# Revit family: IS_Tesi_A6557_BIM_DE
name_source: partatom
category: Plumbing Fixtures
revit_build: Autodesk Revit MEP 2015 (Build: 20140606_1530(x64)
units: mm (PartAtom-declared; Revit-internal decimal feet)

## types (1)
- A6557AA - TESI single lever basin mixer with pop-up waste
    Assembly Code = C1030200
    BIMobject category = Taps & Mixers
    BOSUseNativeGeometries = 1
    Brand url = http://www.idealstandard.co.uk
    Description = A6557AA TESI single lever basin mixer with pop-up waste
    EAN code = https://4015413338226
    Edition number = 1
    FaucetFunction = mixed
    FaucetOperation = leverhandle
    IFC Classification = Valve
    IfcExportAs = Valve
    IfcExportType = BRASSWARE BASIN
    Installation instructions = http://www.idealspec.co.uk
    Manufacturer name = Ideal Standard
    Material = Brass
    Material main = Brass
    Model = A6557AA
    ModelNumber = A6557AA
    Name = TESI single lever basin mixer with pop-up waste
    NettWeight = 1,52 kg
    Nominal height = 159
    Nominal width = 50
    NominalDepth = 0 mm  [stored 0 ft]
    NominalHeight = 159 mm  [stored 0.521654 ft]
    NominalLength = 152 mm
    NominalWidth = 50 mm  [stored 0.164042 ft]
    OmniClass Code = 23.45.55.17
    OmniClass Description = Mixing Faucets
    Product Guid = 306a8794-8d6c-431e-8740-e9c312f102fd
    Product SKU = A6557
    Product data url = https://bimobject.com
    Product family = TESI
    Product group = Basin Mixer
    Product name = TESI - Basin Mixer  Chrome Pu/Met 5L/Min
    Product url = http://www.idealspec.co.uk
    QR code = http://bimobject.com
    Shape = Sculptured
    Size = 159x159x50 mm
    Space = internal
    SpareParts = www.idealstandard.de/ersatzteile
    Technical description = www.idealstandard.de\produkte
    TestPressure = 10 bar
    URL = www.idealstandard.de\produkte
    Uniclass 2015 Code = Pr_40_20_87_98
    Uniclass 2015 Name = Washbasin taps
    ValveMechanism = ceramic disc
    ValveOperation = lever
    VolumeUnits = Litres
    WarrantyDurationParts = 5
    WarrantyDurationUnit = year
    Weight Net (Kg) = 1.52
    WorkingPressure = 1-5 bar

note: [stored X ft] marks values corroborated as IEEE doubles in the binary element streams (Revit-internal decimal feet)

## geometry (parser evidence)
native form markers: Blend x4, Sweep x1
no freeform markers — native parametric forms only
